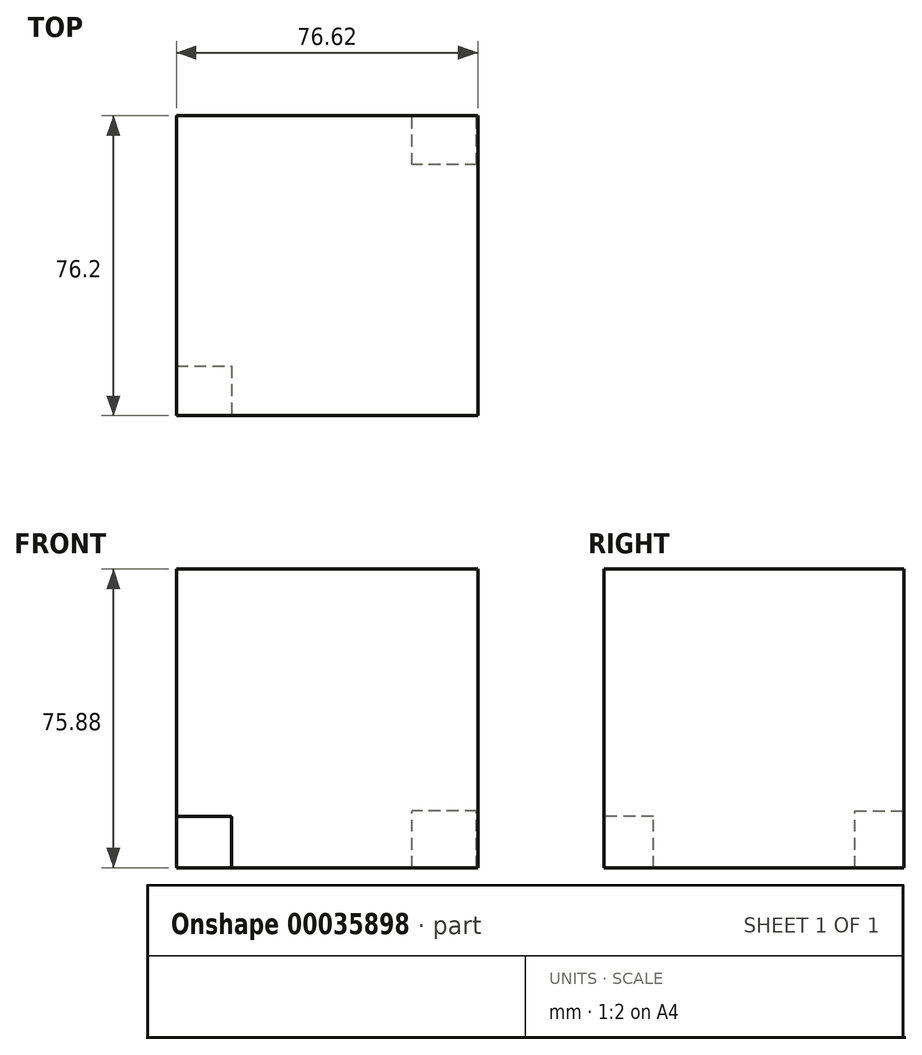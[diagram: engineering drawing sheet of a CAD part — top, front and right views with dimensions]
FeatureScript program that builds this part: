
annotation { "Feature Type Name" : "Feature", "Feature Type Description" : "" }
export const myFeature = defineFeature(function(context is Context, id is Id, definition is map)
    precondition{}
    {
        {
            var Q0;
            Q0=qCreatedBy(makeId("Front.planeOp"),FACE);
            var sketch = newSketch(context, id + "F0", { "sketchPlane" : qUnion([Q0])});
            skLineSegment(sketch, "E0.bottom", {"start": v(0, 0) * mm, "end": v(76.62, 0) * mm});
            skLineSegment(sketch, "E0.top", {"start": v(0, 75.88) * mm, "end": v(76.62, 75.88) * mm});
            skLineSegment(sketch, "E0.left", {"start": v(0, 0) * mm, "end": v(0, 75.88) * mm});
            skLineSegment(sketch, "E0.right", {"start": v(76.62, 0) * mm, "end": v(76.62, 75.88) * mm});
            skSolve(sketch);
        }
        {
            var Q0;
            Q0=makeQuery(id+"F0.imprint","IMPRINT",FACE,{"disambiguationData":[TD([[makeQuery(id+"F0.imprint","IMPRINT",EDGE,{"derivedFrom":sQuery(id+"F0.wireOp",EDGE,"E0.bottom")}),1.0]])]});
            extrude(context, id + "F1", {"entities" : qUnion([Q0]), "depth" : 76.2 * mm});
        }
        {
            var Q0;
            Q0=makeQuery(id+"F1.opExtrude","CAP_FACE",FACE,{"disambiguationData":[OSD([sQuery(id+"F0.wireOp",EDGE,"E0.bottom"),sQuery(id+"F0.wireOp",EDGE,"E0.top"),sQuery(id+"F0.wireOp",EDGE,"E0.left"),sQuery(id+"F0.wireOp",EDGE,"E0.right")])],"isStart":false});
            var sketch = newSketch(context, id + "F2", { "sketchPlane" : qUnion([Q0])});
            skLineSegment(sketch, "E1.bottom", {"start": v(0, 0) * mm, "end": v(14, 0) * mm});
            skLineSegment(sketch, "E1.top", {"start": v(0, 13.1) * mm, "end": v(14, 13.1) * mm});
            skLineSegment(sketch, "E1.left", {"start": v(0, 0) * mm, "end": v(0, 13.1) * mm});
            skLineSegment(sketch, "E1.right", {"start": v(14, 0) * mm, "end": v(14, 13.1) * mm});
            skSolve(sketch);
        }
        {
            var Q0;
            Q0=makeQuery(id+"F2.imprint","IMPRINT",FACE,{"disambiguationData":[TD([[makeQuery(id+"F2.imprint","IMPRINT",EDGE,{"derivedFrom":sQuery(id+"F2.wireOp",EDGE,"E1.bottom")}),1.0]])]});
            extrude(context, id + "F3", {"entities" : qUnion([Q0]), "operationType" : NewBodyOperationType.REMOVE, "oppositeDirection" : true, "depth" : 12.57 * mm});
        }
        {
            var Q0;
            Q0=qCreatedBy(makeId("Front.planeOp"),FACE);
            var sketch = newSketch(context, id + "F4", { "sketchPlane" : qUnion([Q0])});
            skLineSegment(sketch, "E2.bottom", {"start": v(76.29, 0) * mm, "end": v(59.82, 0) * mm});
            skLineSegment(sketch, "E2.top", {"start": v(76.29, 14.44) * mm, "end": v(59.82, 14.44) * mm});
            skLineSegment(sketch, "E2.left", {"start": v(76.29, 0) * mm, "end": v(76.29, 14.44) * mm});
            skLineSegment(sketch, "E2.right", {"start": v(59.82, 0) * mm, "end": v(59.82, 14.44) * mm});
            skSolve(sketch);
        }
        {
            var Q0;
            Q0=makeQuery(id+"F4.imprint","IMPRINT",FACE,{"disambiguationData":[TD([[makeQuery(id+"F4.imprint","IMPRINT",EDGE,{"derivedFrom":sQuery(id+"F4.wireOp",EDGE,"E2.bottom")}),-1.0]])]});
            var Q1;
            Q1=sQuery(id+"F4.wireOp",EDGE,"E2.right");
            extrude(context, id + "F5", {"entities" : qUnion([Q0]), "operationType" : NewBodyOperationType.REMOVE, "surfaceEntities" : qUnion([Q1]), "depth" : 12.45 * mm});
        }
    });
